# Revit family: 001_Shower-Haws_Corporation-Combination_Unit_8317
name_source: partatom
category: Plumbing Fixtures
units: mm (PartAtom-declared; Revit-internal decimal feet)

## family parameters
Always vertical = Yes
Cut with Voids When Loaded = No
OmniClass Number = 23.45.05.14.17
OmniClass Title = Showers
Part Type = Normal
Room Calculation Point = No
Round Connector Dimension = Use Radius
Shared = No
Work Plane-Based = No

## types (2) — shared parameters
Apparent Load = 0 VA
Assembly Code = D2010710
CW Connection = Yes
CWFU = 1
Connector Description = Power Connection
Default Elevation = 0"
Depth = 36 1/2"
Description = Traditional eyewashes irrigate from the outside edge of the eye back toward the nose
Eye Face wash head = 41 3/4"
Fixture = Haws Corporation - Metal - Green Powder Coating
Flow = 20 GPM
Frequency = 60 Hz
Full Height = 89 1/4"
HW Connection = No
HWFU = 1
Keynote = 15410
Lever Height = 65 3/8"
Manufacturer = Haws Corporation
Nominal height = 96"
Nominal width = 21"
Number of Poles = 1
Phase = 1
Power Factor = 1
Product Documentation Link = https://www.hawsco.com
Product Page URL = https://www.hawsco.com
Product data url = https://www.bimobject.com
Pull Rod = Haws Corporation - Metal - High Polished Stainless Steel
Sanitary Radius = 5/8"
Shower Arm Overhang = 25"
Shower Head = Haws Corporation - Metal - Green Powder Coating
Supply Radius = 5/8"
Tubing = Haws Corporation - Metal - Galvanized Steel
Type Comments = Combination shower and eye/face wash, with top or bottom supply, 220 VAC, and with AXION MSR™ eye/face wash and showerhead.
Vent Connection = No
WFU = 1
Waste Connection = Yes
Weight Net (Kg) = 120
zero-valued in all types: Cost

## per-type parameters (varying)
| type | URL | Voltage |
| 8317CTFP | https://www.hawsco.com | 120 V |
| 8317CTFP.220V | http://www.hawsco.com | 220 V |

note: column(s) folded — value = type name in every type: Model

## geometry (parser evidence)
native form markers: Sweep x10
no freeform markers — native parametric forms only
